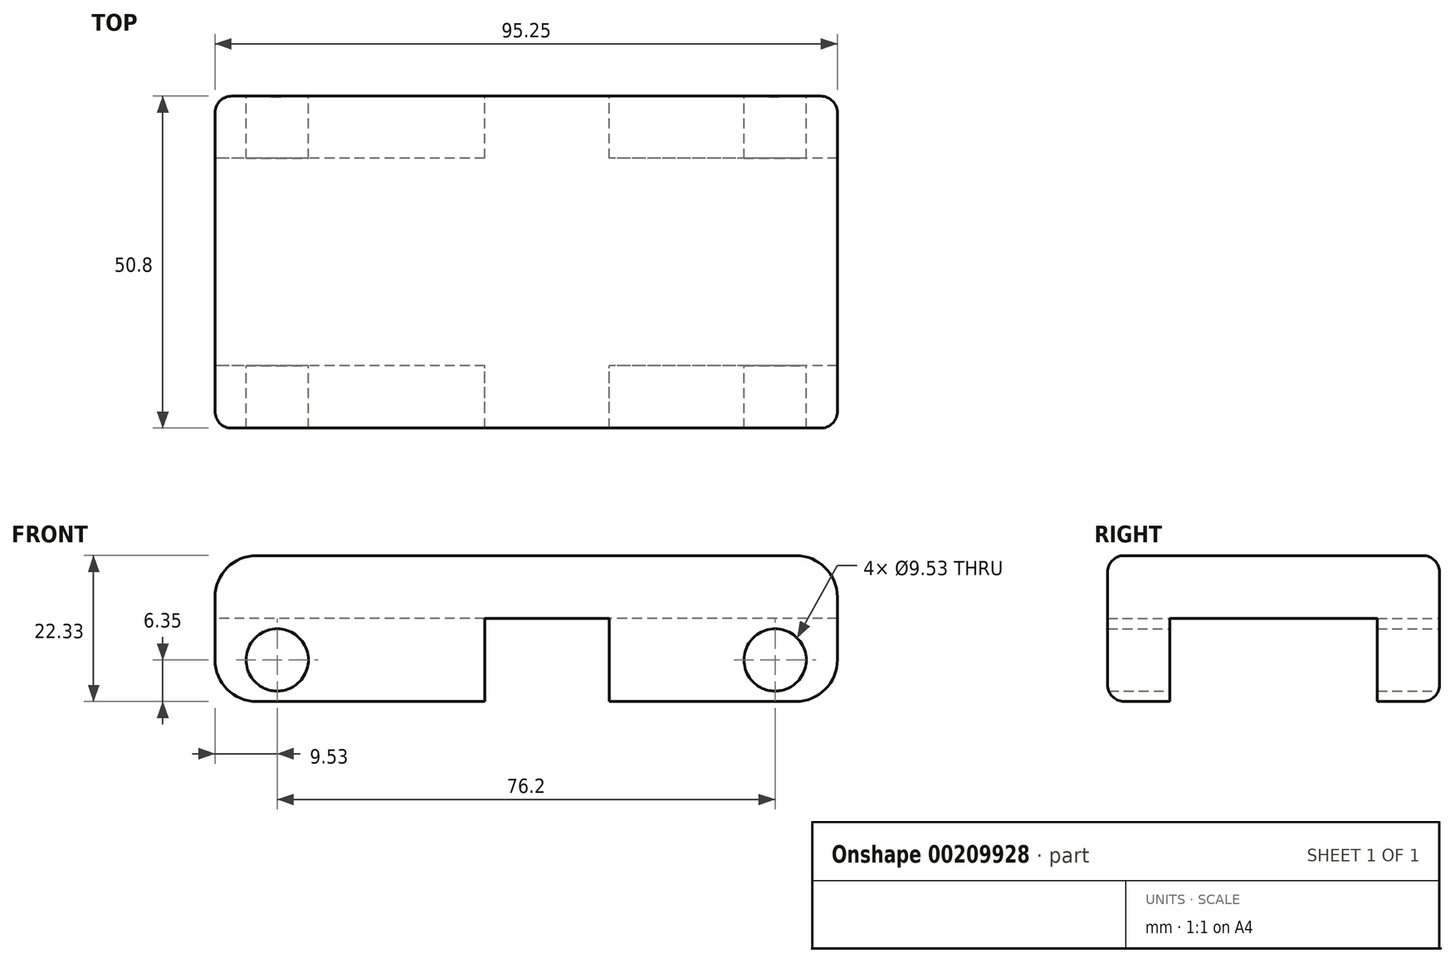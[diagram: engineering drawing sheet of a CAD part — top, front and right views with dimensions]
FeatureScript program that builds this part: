
annotation { "Feature Type Name" : "Feature", "Feature Type Description" : "" }
export const myFeature = defineFeature(function(context is Context, id is Id, definition is map)
    precondition{}
    {
        {
            var Q0;
            Q0=qCreatedBy(makeId("Front.planeOp"),FACE);
            var sketch = newSketch(context, id + "F0", { "sketchPlane" : qUnion([Q0])});
            skCircle(sketch, "E0", {"center": v(-38.1, 0) * mm, "radius": 4.76 * mm});
            skCircle(sketch, "E1", {"center": v(38.1, 0) * mm, "radius": 4.76 * mm});
            skLineSegment(sketch, "E2", {"start": v(-38.1, 0) * mm, "end": v(38.1, 0) * mm, "construction": true});
            skPoint(sketch, "E3", {"position": v(0, 0) * mm});
            skLineSegment(sketch, "E4.bottom", {"start": v(-41.28, 15.98) * mm, "end": v(41.28, 15.98) * mm});
            skLineSegment(sketch, "E4.left", {"start": v(-47.63, 9.63) * mm, "end": v(-47.63, 0) * mm});
            skLineSegment(sketch, "E4.right", {"start": v(47.63, 9.63) * mm, "end": v(47.63, 0) * mm});
            skPoint(sketch, "E5", {"position": v(0, 15.98) * mm});
            skLineSegment(sketch, "E6.bottom", {"start": v(12.7, 6.35) * mm, "end": v(-6.35, 6.35) * mm});
            skLineSegment(sketch, "E6.left", {"start": v(12.7, 6.35) * mm, "end": v(12.7, -6.35) * mm});
            skLineSegment(sketch, "E6.right", {"start": v(-6.35, 6.35) * mm, "end": v(-6.35, -6.35) * mm});
            skPoint(sketch, "E7", {"position": v(-6.35, 0) * mm});
            skPoint(sketch, "E8.visualSharp", {"position": v(-47.63, 15.98) * mm});
            skArc(sketch, "E8.filletArc", {"start": v(-41.28, 15.98) * mm, "mid": v(-45.77, 14.12) * mm, "end": v(-47.63, 9.63) * mm});
            skArc(sketch, "E9.filletArc", {"start": v(-47.63, 0) * mm, "mid": v(-45.77, -4.5) * mm, "end": v(-41.28, -6.35) * mm});
            skArc(sketch, "E10.filletArc", {"start": v(41.28, -6.35) * mm, "mid": v(45.77, -4.5) * mm, "end": v(47.63, 0) * mm});
            skPoint(sketch, "E11.visualSharp", {"position": v(47.62, 15.98) * mm});
            skArc(sketch, "E11.filletArc", {"start": v(47.63, 9.63) * mm, "mid": v(45.77, 14.12) * mm, "end": v(41.28, 15.98) * mm});
            skLineSegment(sketch, "E12", {"start": v(-41.28, -6.35) * mm, "end": v(-6.35, -6.35) * mm});
            skLineSegment(sketch, "E13", {"start": v(12.7, -6.35) * mm, "end": v(41.28, -6.35) * mm});
            skSolve(sketch);
        }
        {
            var Q0;
            Q0 = qSketchRegion(id + "F0", true);
            extrude(context, id + "F1", {"entities" : qUnion([Q0]), "endBound" : BoundingType.SYMMETRIC, "depth" : 50.8 * mm});
        }
        {
            var Q0;
            Q0=qCreatedBy(makeId("Right.planeOp"),FACE);
            var sketch = newSketch(context, id + "F2", { "sketchPlane" : qUnion([Q0])});
            skLineSegment(sketch, "E14.bottom", {"start": v(-15.88, 6.35) * mm, "end": v(15.88, 6.35) * mm});
            skLineSegment(sketch, "E14.top", {"start": v(-15.88, -6.35) * mm, "end": v(15.88, -6.35) * mm});
            skLineSegment(sketch, "E14.left", {"start": v(-15.88, 6.35) * mm, "end": v(-15.88, -6.35) * mm});
            skLineSegment(sketch, "E14.right", {"start": v(15.88, 6.35) * mm, "end": v(15.88, -6.35) * mm});
            skPoint(sketch, "E15", {"position": v(0, -6.35) * mm});
            skSolve(sketch);
        }
        {
            var Q0;
            Q0 = qSketchRegion(id + "F2", true);
            extrude(context, id + "F3", {"entities" : qUnion([Q0]), "operationType" : NewBodyOperationType.REMOVE, "endBound" : BoundingType.THROUGH_ALL, "depth" : 25.4 * mm, "hasSecondDirection" : true, "secondDirectionBound" : SecondDirectionBoundingType.THROUGH_ALL, "secondDirectionOppositeDirection" : true, "secondDirectionDepth" : 25.4 * mm});
        }
        {
            var Q0;
            Q0=makeQuery(id+"F1.opExtrude","CAP_EDGE",EDGE,{"disambiguationData":[OSD([sQuery(id+"F0.wireOp",EDGE,"E4.bottom")])],"isStart":true});
            var Q1;
            Q1=makeQuery(id+"F1.opExtrude","CAP_EDGE",EDGE,{"disambiguationData":[OSD([sQuery(id+"F0.wireOp",EDGE,"E4.bottom")])],"isStart":false});
            fillet(context, id + "F4", {"entities" : qUnion([Q0, Q1]), "radius" : 2.54 * mm, "tangentPropagation" : true, "allowEdgeOverflow" : false});
        }
    });
